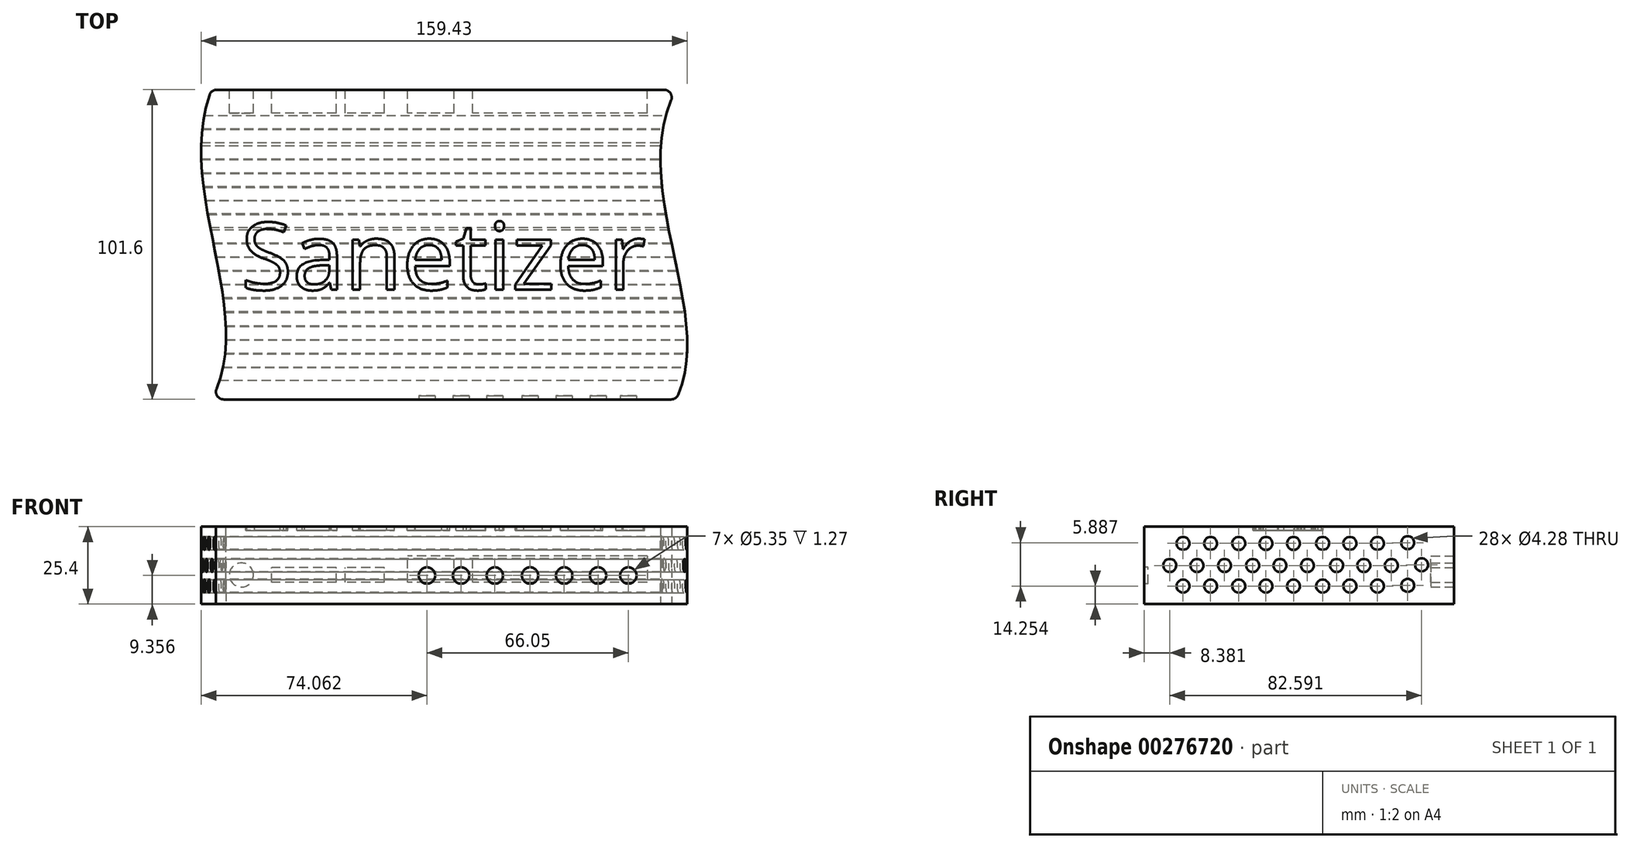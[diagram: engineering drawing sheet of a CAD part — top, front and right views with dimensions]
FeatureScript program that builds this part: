
annotation { "Feature Type Name" : "Feature", "Feature Type Description" : "" }
export const myFeature = defineFeature(function(context is Context, id is Id, definition is map)
    precondition{}
    {
        {
            var Q0;
            Q0=qCreatedBy(makeId("Top.planeOp"),FACE);
            var sketch = newSketch(context, id + "F0", { "sketchPlane" : qUnion([Q0])});
            skLineSegment(sketch, "E0.bottom", {"start": v(-45.42, -35.98) * mm, "end": v(106.98, -35.98) * mm});
            skLineSegment(sketch, "E0.top", {"start": v(-45.42, 65.62) * mm, "end": v(106.98, 65.62) * mm});
            skFitSpline(sketch, "E1", {"points": [v(-45.42, 65.62) * mm, v(-45.42, -35.98) * mm], "startDerivative": vector(-37.93, -99) * mm, "endDerivative": vector(-46.54, -85.13) * mm});
            skFitSpline(sketch, "E2", {"points": [v(106.98, 65.62) * mm, v(106.98, -35.98) * mm], "startDerivative": vector(-49.91, -94.67) * mm, "endDerivative": vector(-41.07, -83.56) * mm});
            skSolve(sketch);
        }
        {
            var Q0;
            Q0=makeQuery(id+"F0.imprint","IMPRINT",FACE,{"disambiguationData":[TD([[makeQuery(id+"F0.imprint","IMPRINT",EDGE,{"derivedFrom":sQuery(id+"F0.wireOp",EDGE,"E0.bottom")}),1.0]])]});
            extrude(context, id + "F1", {"entities" : qUnion([Q0]), "depth" : 25.4 * mm});
        }
        {
            var Q0;
            Q0=makeQuery(id+"F1.opExtrude","SWEPT_EDGE",EDGE,{"disambiguationData":[OSD([sQuery(id+"F0.wireOp",EDGE,"E0.top"),sQuery(id+"F0.wireOp",EDGE,"E2")])]});
            var Q1;
            Q1=makeQuery(id+"F1.opExtrude","SWEPT_EDGE",EDGE,{"disambiguationData":[OSD([sQuery(id+"F0.wireOp",EDGE,"E0.bottom"),sQuery(id+"F0.wireOp",EDGE,"E1")])]});
            var Q2;
            Q2=makeQuery(id+"F1.opExtrude","SWEPT_EDGE",EDGE,{"disambiguationData":[OSD([sQuery(id+"F0.wireOp",EDGE,"E0.top"),sQuery(id+"F0.wireOp",EDGE,"E1")])]});
            var Q3;
            Q3=makeQuery(id+"F1.opExtrude","SWEPT_EDGE",EDGE,{"disambiguationData":[OSD([sQuery(id+"F0.wireOp",EDGE,"E0.bottom"),sQuery(id+"F0.wireOp",EDGE,"E2")])]});
            fillet(context, id + "F2", {"entities" : qUnion([Q0, Q1, Q2, Q3]), "radius" : 2.54 * mm, "tangentPropagation" : true, "allowEdgeOverflow" : false});
        }
        {
            var Q0;
            Q0=makeQuery(id+"F1.opExtrude","CAP_FACE",FACE,{"disambiguationData":[OSD([sQuery(id+"F0.wireOp",EDGE,"E0.bottom"),sQuery(id+"F0.wireOp",EDGE,"E0.top"),sQuery(id+"F0.wireOp",EDGE,"E1"),sQuery(id+"F0.wireOp",EDGE,"E2")])],"isStart":false});
            var sketch = newSketch(context, id + "F3", { "sketchPlane" : qUnion([Q0])});
            skText(sketch, "E3", { "text": "Sanetizer\n", "fontName": "OpenSans-Regular.ttf"});
            const initialGuessF3  = {"E3": [-0.03572, 0, 1, 0, 0.02212]};
            skSetInitialGuess(sketch, initialGuessF3);
            skSolve(sketch);
        }
        {
            var Q0;
            Q0 = qSketchRegion(id + "F3", true);
            extrude(context, id + "F4", {"entities" : qUnion([Q0]), "operationType" : NewBodyOperationType.REMOVE, "oppositeDirection" : true, "depth" : 1.27 * mm});
        }
        {
            var Q0;
            Q0=qCreatedBy(makeId("Right.planeOp"),FACE);
            var sketch = newSketch(context, id + "F5", { "sketchPlane" : qUnion([Q0])});
            skLineSegment(sketch, "E4", {"start": v(-34.37, 12.65) * mm, "end": v(62.02, 12.65) * mm});
            skLineSegment(sketch, "E5", {"start": v(-34.48, 5.93) * mm, "end": v(61.8, 5.93) * mm});
            skCircle(sketch, "E6", {"center": v(-14.21, 19.92) * mm, "radius": 2.14 * mm});
            skCircle(sketch, "E7", {"center": v(-23.25, 19.92) * mm, "radius": 2.14 * mm});
            skCircle(sketch, "E8", {"center": v(-4.98, 19.92) * mm, "radius": 2.14 * mm});
            skCircle(sketch, "E9", {"center": v(12.97, 19.92) * mm, "radius": 2.14 * mm});
            skCircle(sketch, "E10", {"center": v(3.94, 19.92) * mm, "radius": 2.14 * mm});
            skCircle(sketch, "E11", {"center": v(22.55, 19.92) * mm, "radius": 2.14 * mm});
            skCircle(sketch, "E12", {"center": v(40.5, 19.92) * mm, "radius": 2.14 * mm});
            skCircle(sketch, "E13", {"center": v(31.47, 19.92) * mm, "radius": 2.14 * mm});
            skCircle(sketch, "E14", {"center": v(50.42, 20.14) * mm, "radius": 2.14 * mm});
            skCircle(sketch, "E15", {"center": v(-27.6, 12.65) * mm, "radius": 2.14 * mm});
            skCircle(sketch, "E16", {"center": v(-9.64, 12.65) * mm, "radius": 2.14 * mm});
            skCircle(sketch, "E17", {"center": v(-18.68, 12.65) * mm, "radius": 2.14 * mm});
            skCircle(sketch, "E18", {"center": v(-0.41, 12.65) * mm, "radius": 2.14 * mm});
            skCircle(sketch, "E19", {"center": v(17.55, 12.65) * mm, "radius": 2.14 * mm});
            skCircle(sketch, "E20", {"center": v(8.51, 12.65) * mm, "radius": 2.14 * mm});
            skCircle(sketch, "E21", {"center": v(27.12, 12.65) * mm, "radius": 2.14 * mm});
            skCircle(sketch, "E22", {"center": v(45.08, 12.65) * mm, "radius": 2.14 * mm});
            skCircle(sketch, "E23", {"center": v(36.04, 12.65) * mm, "radius": 2.14 * mm});
            skCircle(sketch, "E24", {"center": v(55, 12.87) * mm, "radius": 2.14 * mm});
            skCircle(sketch, "E25", {"center": v(-14.21, 5.9) * mm, "radius": 2.14 * mm});
            skCircle(sketch, "E26", {"center": v(-23.25, 5.9) * mm, "radius": 2.14 * mm});
            skCircle(sketch, "E27", {"center": v(-4.98, 5.89) * mm, "radius": 2.14 * mm});
            skCircle(sketch, "E28", {"center": v(12.97, 5.89) * mm, "radius": 2.14 * mm});
            skCircle(sketch, "E29", {"center": v(3.94, 5.89) * mm, "radius": 2.14 * mm});
            skCircle(sketch, "E30", {"center": v(22.55, 5.9) * mm, "radius": 2.14 * mm});
            skCircle(sketch, "E31", {"center": v(40.5, 5.9) * mm, "radius": 2.14 * mm});
            skCircle(sketch, "E32", {"center": v(31.47, 5.9) * mm, "radius": 2.14 * mm});
            skCircle(sketch, "E33", {"center": v(50.42, 6.11) * mm, "radius": 2.14 * mm});
            skSolve(sketch);
        }
        {
            var Q0;
            Q0 = qSketchRegion(id + "F5", true);
            extrude(context, id + "F6", {"entities" : qUnion([Q0]), "operationType" : NewBodyOperationType.REMOVE, "oppositeDirection" : true, "depth" : 87.38 * mm, "hasSecondDirection" : true, "secondDirectionOppositeDirection" : false, "secondDirectionDepth" : 113.54 * mm});
        }
        {
            var Q0;
            Q0=makeQuery(id+"F1.opExtrude","SWEPT_FACE",FACE,{"disambiguationData":[OSD([sQuery(id+"F0.wireOp",EDGE,"E0.top")])]});
            var sketch = newSketch(context, id + "F7", { "sketchPlane" : qUnion([Q0])});
            skLineSegment(sketch, "E34.bottom", {"start": v(-97.5, 15.83) * mm, "end": v(-82.8, 15.83) * mm});
            skLineSegment(sketch, "E34.top", {"start": v(-97.5, 7.08) * mm, "end": v(-82.8, 7.08) * mm});
            skLineSegment(sketch, "E34.left", {"start": v(-97.5, 15.83) * mm, "end": v(-97.5, 7.08) * mm});
            skLineSegment(sketch, "E34.right", {"start": v(-82.8, 15.83) * mm, "end": v(-82.8, 7.08) * mm});
            skLineSegment(sketch, "E35.bottom", {"start": v(-82.8, 7.08) * mm, "end": v(-68.99, 7.08) * mm});
            skLineSegment(sketch, "E35.top", {"start": v(-82.8, 15.83) * mm, "end": v(-68.99, 15.83) * mm});
            skLineSegment(sketch, "E35.left", {"start": v(-82.8, 7.08) * mm, "end": v(-82.8, 15.83) * mm});
            skLineSegment(sketch, "E35.right", {"start": v(-68.99, 7.08) * mm, "end": v(-68.99, 15.83) * mm});
            skLineSegment(sketch, "E36.bottom", {"start": v(-68.99, 7.08) * mm, "end": v(-54.65, 7.08) * mm});
            skLineSegment(sketch, "E36.top", {"start": v(-68.99, 15.83) * mm, "end": v(-54.65, 15.83) * mm});
            skLineSegment(sketch, "E36.right", {"start": v(-54.65, 7.08) * mm, "end": v(-54.65, 15.83) * mm});
            skLineSegment(sketch, "E37.bottom", {"start": v(-54.65, 7.08) * mm, "end": v(-40.3, 7.08) * mm});
            skLineSegment(sketch, "E37.top", {"start": v(-54.65, 15.83) * mm, "end": v(-40.3, 15.83) * mm});
            skLineSegment(sketch, "E37.right", {"start": v(-40.3, 7.08) * mm, "end": v(-40.3, 15.83) * mm});
            skLineSegment(sketch, "E38.bottom", {"start": v(-34.18, 7.08) * mm, "end": v(-18.97, 7.08) * mm});
            skLineSegment(sketch, "E38.top", {"start": v(-34.18, 15.83) * mm, "end": v(-18.97, 15.83) * mm});
            skLineSegment(sketch, "E38.left", {"start": v(-34.18, 7.08) * mm, "end": v(-34.18, 15.83) * mm});
            skLineSegment(sketch, "E38.right", {"start": v(-18.97, 7.08) * mm, "end": v(-18.97, 15.83) * mm});
            skLineSegment(sketch, "E39.bottom", {"start": v(-11.28, 7.08) * mm, "end": v(1.5, 7.08) * mm});
            skLineSegment(sketch, "E39.top", {"start": v(-11.28, 11.98) * mm, "end": v(1.5, 11.98) * mm});
            skLineSegment(sketch, "E39.left", {"start": v(-11.28, 7.08) * mm, "end": v(-11.28, 11.98) * mm});
            skLineSegment(sketch, "E39.right", {"start": v(1.5, 7.08) * mm, "end": v(1.5, 11.98) * mm});
            skLineSegment(sketch, "E40.bottom", {"start": v(4.46, 7.08) * mm, "end": v(25.63, 7.08) * mm});
            skLineSegment(sketch, "E40.top", {"start": v(4.46, 11.98) * mm, "end": v(25.63, 11.98) * mm});
            skLineSegment(sketch, "E40.left", {"start": v(4.46, 7.08) * mm, "end": v(4.46, 11.98) * mm});
            skLineSegment(sketch, "E40.right", {"start": v(25.63, 7.08) * mm, "end": v(25.63, 11.98) * mm});
            skCircle(sketch, "E41", {"center": v(35.6, 9.53) * mm, "radius": 3.96 * mm});
            skPoint(sketch, "E41.centerSnap0", {"position": v(25.63, 9.53) * mm});
            skSolve(sketch);
        }
        {
            var Q0;
            Q0 = qSketchRegion(id + "F7", true);
            extrude(context, id + "F8", {"entities" : qUnion([Q0]), "operationType" : NewBodyOperationType.REMOVE, "oppositeDirection" : true, "depth" : 7.62 * mm});
        }
        {
            var Q0;
            Q0=makeQuery(id+"F1.opExtrude","SWEPT_FACE",FACE,{"disambiguationData":[OSD([sQuery(id+"F0.wireOp",EDGE,"E0.bottom")])]});
            var sketch = newSketch(context, id + "F9", { "sketchPlane" : qUnion([Q0])});
            skCircle(sketch, "E42", {"center": v(36.46, 9.36) * mm, "radius": 2.68 * mm});
            skCircle(sketch, "E43", {"center": v(25.27, 9.36) * mm, "radius": 2.68 * mm});
            skCircle(sketch, "E44", {"center": v(47.53, 9.36) * mm, "radius": 2.68 * mm});
            skCircle(sketch, "E45", {"center": v(70.29, 9.36) * mm, "radius": 2.68 * mm});
            skCircle(sketch, "E46", {"center": v(59.1, 9.36) * mm, "radius": 2.68 * mm});
            skCircle(sketch, "E47", {"center": v(81.36, 9.36) * mm, "radius": 2.68 * mm});
            skCircle(sketch, "E48", {"center": v(91.32, 9.36) * mm, "radius": 2.68 * mm});
            skSolve(sketch);
        }
        {
            var Q0;
            Q0 = qSketchRegion(id + "F9", true);
            extrude(context, id + "F10", {"entities" : qUnion([Q0]), "operationType" : NewBodyOperationType.REMOVE, "oppositeDirection" : true, "depth" : 1.27 * mm});
        }
    });
